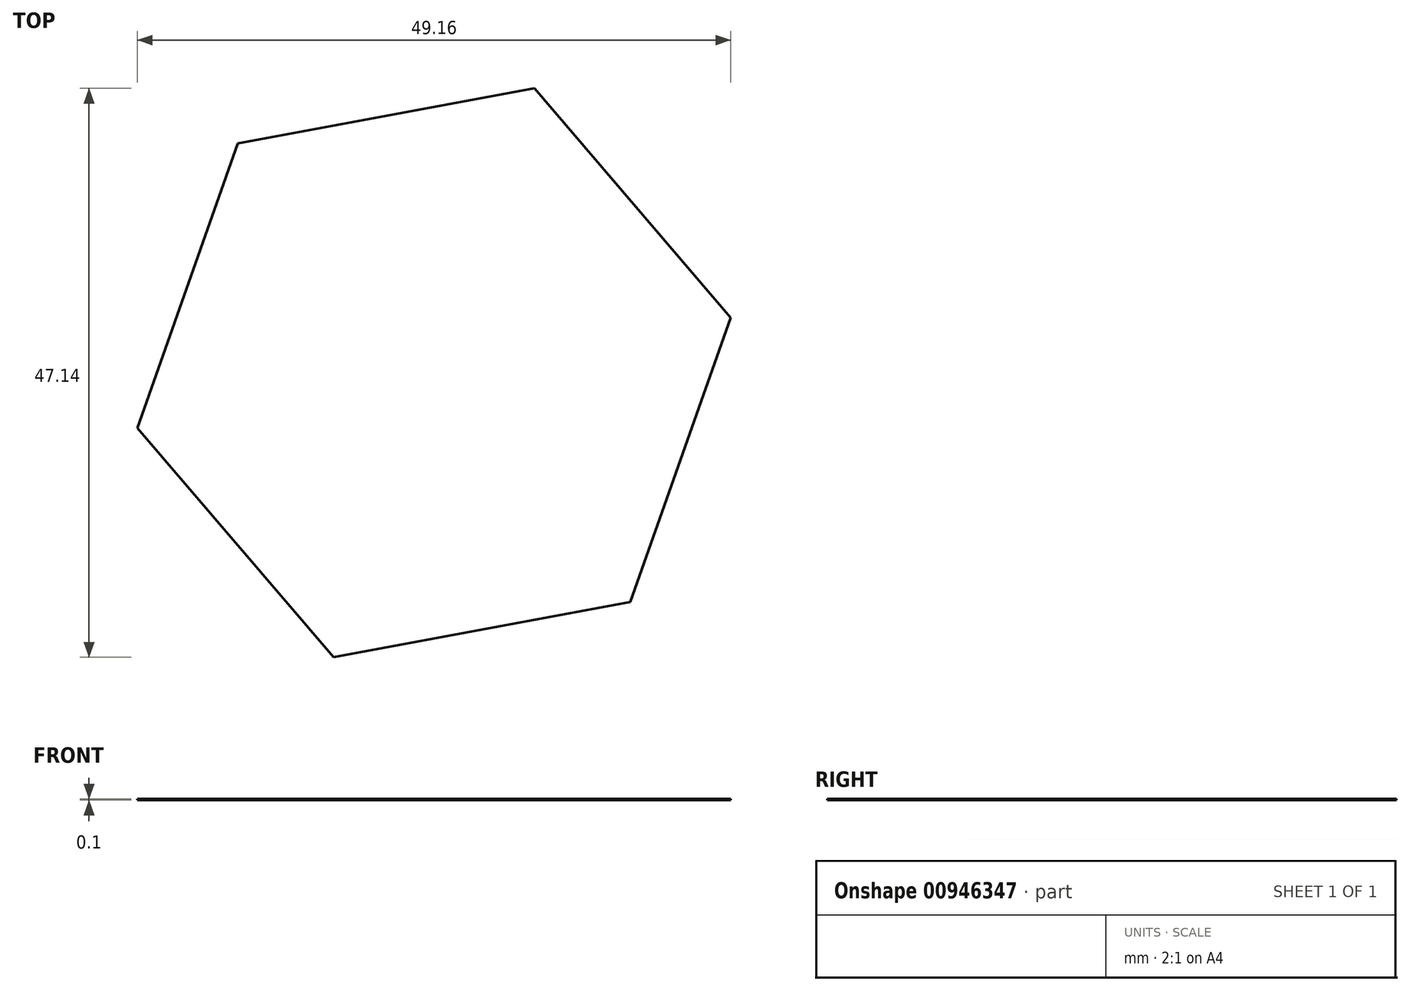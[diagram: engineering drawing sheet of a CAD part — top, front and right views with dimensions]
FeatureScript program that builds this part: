
annotation { "Feature Type Name" : "Feature", "Feature Type Description" : "" }
export const myFeature = defineFeature(function(context is Context, id is Id, definition is map)
    precondition{}
    {
        {
            var Q0;
            Q0=qCreatedBy(makeId("Top.planeOp"),FACE);
            var sketch = newSketch(context, id + "F0", { "sketchPlane" : qUnion([Q0])});
            skCircle(sketch, "E0.cCircle", {"center": v(0, 0) * mm, "radius": 21.65 * mm, "construction": true});
            skLineSegment(sketch, "E0.0", {"start": v(16.25, -19) * mm, "end": v(-8.33, -23.57) * mm});
            skLineSegment(sketch, "E0.1", {"start": v(-8.33, -23.57) * mm, "end": v(-24.58, -4.57) * mm});
            skLineSegment(sketch, "E0.2", {"start": v(-24.58, -4.57) * mm, "end": v(-16.25, 19) * mm});
            skLineSegment(sketch, "E0.3", {"start": v(-16.25, 19) * mm, "end": v(8.33, 23.57) * mm});
            skLineSegment(sketch, "E0.4", {"start": v(8.33, 23.57) * mm, "end": v(24.58, 4.57) * mm});
            skLineSegment(sketch, "E0.5", {"start": v(24.58, 4.57) * mm, "end": v(16.25, -19) * mm});
            skPoint(sketch, "E0.0.midPoint", {"position": v(3.96, -21.29) * mm});
            skSolve(sketch);
        }
        {
            var Q0;
            Q0=makeQuery(id+"F0.imprint","IMPRINT",FACE,{"disambiguationData":[TD([[makeQuery(id+"F0.imprint","IMPRINT",EDGE,{"derivedFrom":sQuery(id+"F0.wireOp",EDGE,"E0.0")}),-1.0]])]});
            extrude(context, id + "F1", {"entities" : qUnion([Q0]), "depth" : 0.1 * mm, "offsetDistance" : 25 * mm});
        }
    });
